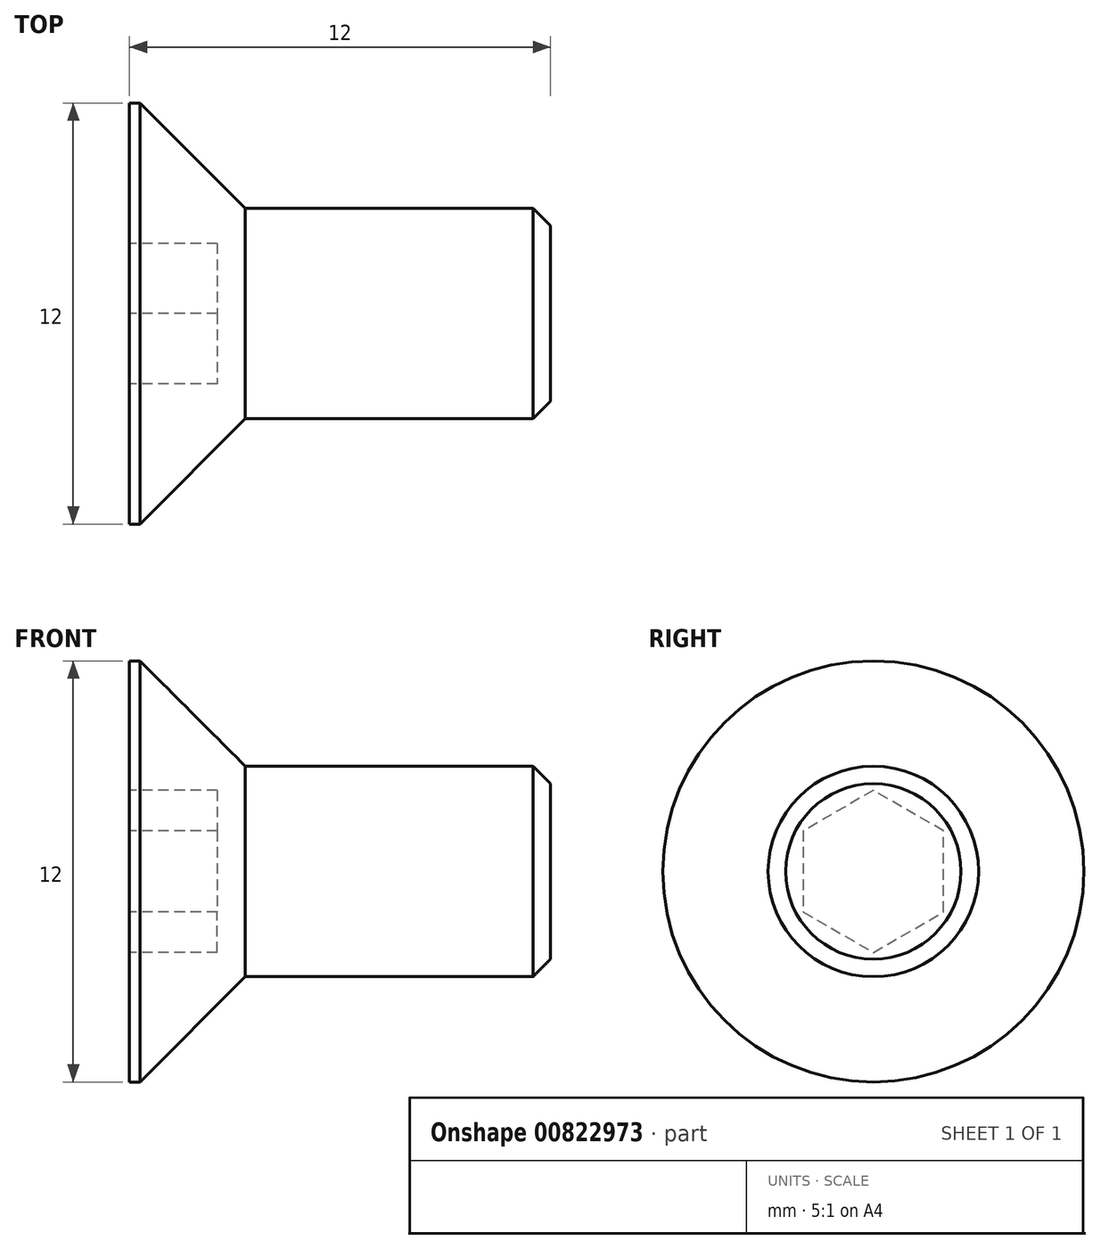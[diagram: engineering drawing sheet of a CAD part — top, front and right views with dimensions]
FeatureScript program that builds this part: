
annotation { "Feature Type Name" : "Feature", "Feature Type Description" : "" }
export const myFeature = defineFeature(function(context is Context, id is Id, definition is map)
    precondition{}
    {
        {
            var Q0;
            Q0=qCreatedBy(makeId("Front.planeOp"),FACE);
            var sketch = newSketch(context, id + "F0", { "sketchPlane" : qUnion([Q0])});
            skLineSegment(sketch, "E0", {"start": v(0, 0) * mm, "end": v(0, 6) * mm});
            skLineSegment(sketch, "E1", {"start": v(3.3, 3) * mm, "end": v(12, 3) * mm});
            skLineSegment(sketch, "E2", {"start": v(12, 3) * mm, "end": v(12, 0) * mm});
            skLineSegment(sketch, "E3", {"start": v(12, 0) * mm, "end": v(0, 0) * mm});
            skLineSegment(sketch, "E4", {"start": v(-3.56, 0) * mm, "end": v(0, 0) * mm, "construction": true});
            skLineSegment(sketch, "E5", {"start": v(0, 6) * mm, "end": v(0.3, 6) * mm});
            skLineSegment(sketch, "E6", {"start": v(0.3, 6) * mm, "end": v(3.3, 3) * mm});
            skSolve(sketch);
        }
        {
            var Q0;
            Q0 = qSketchRegion(id + "F0", true);
            var Q1;
            Q1=sQuery(id+"F0.wireOp",EDGE,"E4");
            revolve(context, id + "F1", {"surfaceOperationType" : NewSurfaceOperationType.NEW, "entities" : qUnion([Q0]), "axis" : qUnion([Q1]), "revolveType" : RevolveType.FULL});
        }
        {
            var Q0;
            Q0=makeQuery(id+"F1.opRevolve","SWEPT_EDGE",EDGE,{"disambiguationData":[OSD([sQuery(id+"F0.wireOp",EDGE,"E1"),sQuery(id+"F0.wireOp",EDGE,"E2")])]});
            chamfer(context, id + "F2", {"entities" : qUnion([Q0]), "width" : 0.5 * mm, "tangentPropagation" : true});
        }
        {
            var Q0;
            Q0=makeQuery(id+"F1.opRevolve","SWEPT_FACE",FACE,{"disambiguationData":[OSD([sQuery(id+"F0.wireOp",EDGE,"E0")])]});
            var sketch = newSketch(context, id + "F3", { "sketchPlane" : qUnion([Q0])});
            skCircle(sketch, "E7.cCircle", {"center": v(0, 0) * mm, "radius": 2 * mm, "construction": true});
            skLineSegment(sketch, "E7.0", {"start": v(2, 1.15) * mm, "end": v(2, -1.15) * mm});
            skLineSegment(sketch, "E7.1", {"start": v(2, -1.15) * mm, "end": v(0, -2.3) * mm});
            skLineSegment(sketch, "E7.2", {"start": v(0, -2.3) * mm, "end": v(-2, -1.15) * mm});
            skLineSegment(sketch, "E7.3", {"start": v(-2, -1.15) * mm, "end": v(-2, 1.15) * mm});
            skLineSegment(sketch, "E7.4", {"start": v(-2, 1.15) * mm, "end": v(0, 2.3) * mm});
            skLineSegment(sketch, "E7.5", {"start": v(0, 2.3) * mm, "end": v(2, 1.15) * mm});
            skPoint(sketch, "E7.0.midPoint", {"position": v(2, 0) * mm});
            skSolve(sketch);
        }
        {
            var Q0;
            Q0 = qSketchRegion(id + "F3", true);
            extrude(context, id + "F4", {"entities" : qUnion([Q0]), "operationType" : NewBodyOperationType.REMOVE, "oppositeDirection" : true, "depth" : 2.5 * mm, "offsetDistance" : 25 * mm});
        }
    });
